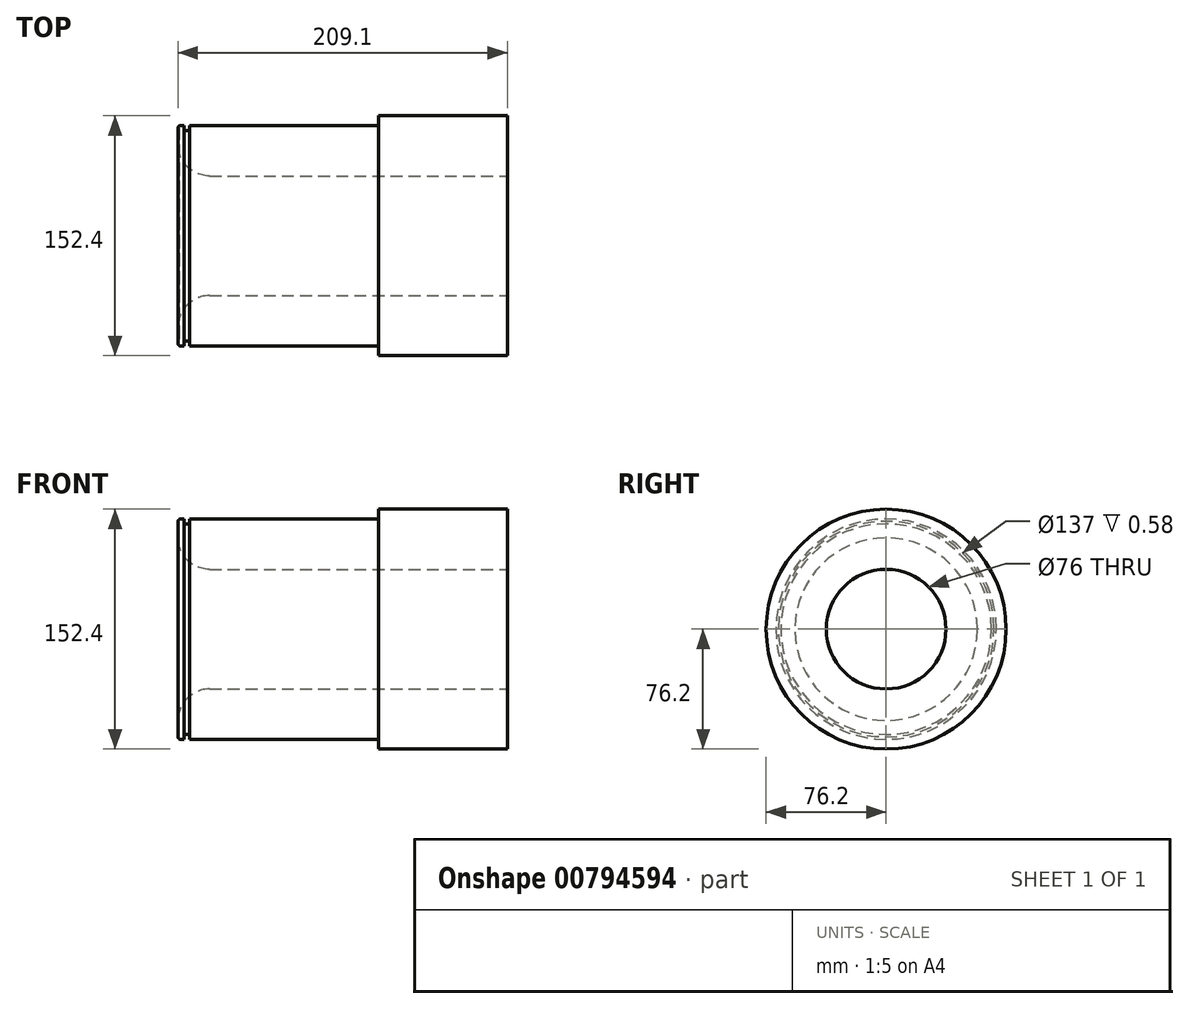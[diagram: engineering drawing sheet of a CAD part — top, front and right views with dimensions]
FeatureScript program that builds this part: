
annotation { "Feature Type Name" : "Feature", "Feature Type Description" : "" }
export const myFeature = defineFeature(function(context is Context, id is Id, definition is map)
    precondition{}
    {
        {
            var Q0;
            Q0=qCreatedBy(makeId("Front.planeOp"),FACE);
            var sketch = newSketch(context, id + "F0", { "sketchPlane" : qUnion([Q0])});
            skLineSegment(sketch, "E0", {"start": v(0, 0) * mm, "end": v(-357.8, 0) * mm, "construction": true});
            skLineSegment(sketch, "E1", {"start": v(0, 38) * mm, "end": v(-189.1, 38) * mm});
            skLineSegment(sketch, "E2", {"start": v(0, 76.2) * mm, "end": v(-82.5, 76.2) * mm});
            skLineSegment(sketch, "E3", {"start": v(0, 76.2) * mm, "end": v(0, 38) * mm});
            skLineSegment(sketch, "E4", {"start": v(-82.5, 70) * mm, "end": v(-201.92, 70) * mm});
            skLineSegment(sketch, "E5", {"start": v(-82.5, 76.2) * mm, "end": v(-82.5, 70) * mm});
            skLineSegment(sketch, "E6", {"start": v(-201.92, 66.87) * mm, "end": v(-205.45, 66.87) * mm});
            skLineSegment(sketch, "E7", {"start": v(-201.92, 70) * mm, "end": v(-201.92, 66.87) * mm});
            skLineSegment(sketch, "E8", {"start": v(-205.45, 66.87) * mm, "end": v(-205.45, 70) * mm});
            skLineSegment(sketch, "E9", {"start": v(-209.1, 58) * mm, "end": v(-209.1, 68.5) * mm});
            skLineSegment(sketch, "E10", {"start": v(-207.6, 70) * mm, "end": v(-205.45, 70) * mm});
            skPoint(sketch, "E11.visualSharp", {"position": v(-209.1, 70) * mm});
            skArc(sketch, "E11.filletArc", {"start": v(-207.6, 70) * mm, "mid": v(-208.66, 69.56) * mm, "end": v(-209.1, 68.5) * mm});
            skPoint(sketch, "E12.visualSharp", {"position": v(-209.1, 38) * mm});
            skArc(sketch, "E12.filletArc", {"start": v(-209.1, 58) * mm, "mid": v(-203.24, 43.86) * mm, "end": v(-189.1, 38) * mm});
            skSolve(sketch);
        }
        {
            var Q0;
            Q0 = qSketchRegion(id + "F0", true);
            var Q1;
            Q1=sQuery(id+"F0.wireOp",EDGE,"E0");
            revolve(context, id + "F1", {"surfaceOperationType" : NewSurfaceOperationType.NEW, "entities" : qUnion([Q0]), "axis" : qUnion([Q1]), "revolveType" : RevolveType.FULL});
        }
        {
            var Q0;
            Q0=makeQuery(id+"F1.opRevolve","SWEPT_FACE",FACE,{"disambiguationData":[OSD([sQuery(id+"F0.wireOp",EDGE,"E9")])]});
            var Q1;
            Q1=makeQuery(id+"F1.opRevolve","SWEPT_FACE",FACE,{"disambiguationData":[OSD([sQuery(id+"F0.wireOp",EDGE,"E5")])]});
            extrude(context, id + "F2", {"entities" : qUnion([Q0, Q1]), "operationType" : NewBodyOperationType.REMOVE, "oppositeDirection" : true, "depth" : .58 * mm, "offsetDistance" : 25 * mm});
        }
    });
